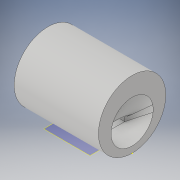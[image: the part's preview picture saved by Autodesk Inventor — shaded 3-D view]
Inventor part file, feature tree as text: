
AUTODESK INVENTOR PART (.ipt)
format: ipt  version: 2019 (Build 230136000, 136)  size: 234,496 bytes
history: native  units: in
note: dims shown in document units (in); Inventor stores cm internally (conversion verified against a paired STEP export)
features: sketch x7, extrude x2, revolve x1, loft x1, fillet x1, plane x1, other x1
ambient origin geometry x8: Origin, YZ Plane, XZ Plane, XY Plane, X Axis, Y Axis, Z Axis, Center Point
bodies: Solid1 (feature_tree)
feature tree (14):
  revolve  "Revolution1"  [1 undecoded]
  sketch  "Sketch2"  dims[d3=0.7874in d4=90.0deg]
  extrude  "Extrusion1"  TaperAngle=90.0deg  [1 undecoded]
  sketch  "Sketch4"  dims[d9=0.7874in d10=0.0in d11=90.0deg]
  sketch  "Sketch5"  dims[d12=0.0in d13=90.0deg]
  loft  "Loft1"
  fillet  "Fillet1"  Radius=0.3937in
  sketch  "Sketch6"  dims[d14=0.2362in]
  plane  "Work Plane1"
  extrude  "Extrusion2"  TaperAngle=0.0deg  [1 undecoded]
  sketch  "Sketch1"  dims[d0=0.1181in d1=0.7874in]
  sketch  "Sketch3"  dims[d5=0.0591in d6=0.5118in d7=0.3937in d8=0.0in]
  other  "Edges1"
  sketch  "Sketch7"  dims[d15=0.5118in d16=0.1969in d17=0.0in d18=0.6299in d19=0.7177in]
note: 3 required parameter values undecoded (feature->parameter linkage not recoverable at this tier; creation-order binding heuristic only, values carry confidence <= 0.55)